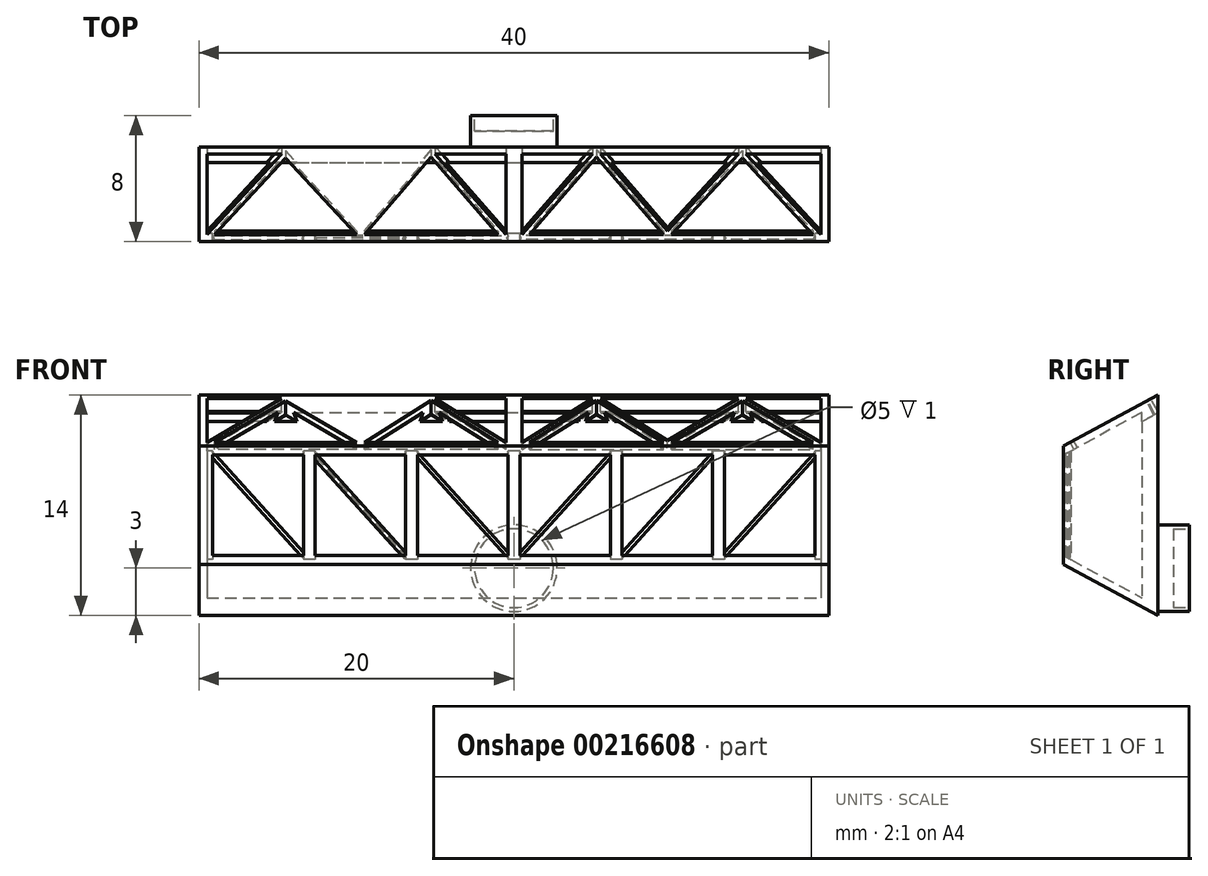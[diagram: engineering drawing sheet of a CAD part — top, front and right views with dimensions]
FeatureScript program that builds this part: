
annotation { "Feature Type Name" : "Feature", "Feature Type Description" : "" }
export const myFeature = defineFeature(function(context is Context, id is Id, definition is map)
    precondition{}
    {
        {
            var Q0;
            Q0=qCreatedBy(makeId("Right.planeOp"),FACE);
            var sketch = newSketch(context, id + "F0", { "sketchPlane" : qUnion([Q0])});
            skLineSegment(sketch, "E0", {"start": v(0, 0) * mm, "end": v(0, 7) * mm});
            skLineSegment(sketch, "E1", {"start": v(0, 0) * mm, "end": v(0, -7) * mm});
            skLineSegment(sketch, "E2", {"start": v(0, 0) * mm, "end": v(-6, 0) * mm});
            skLineSegment(sketch, "E3", {"start": v(-6, 0) * mm, "end": v(-6, 3.75) * mm});
            skLineSegment(sketch, "E4", {"start": v(-6, 3.75) * mm, "end": v(0, 7) * mm});
            skLineSegment(sketch, "E5.MirrorCS", {"start": v(-6, 0) * mm, "end": v(-6, -3.75) * mm});
            skLineSegment(sketch, "E6", {"start": v(-6, -3.75) * mm, "end": v(0, -7) * mm});
            skSolve(sketch);
        }
        {
            var Q0;
            Q0=makeQuery(id+"F0.imprint","IMPRINT",FACE,{"disambiguationData":[TD([[makeQuery(id+"F0.imprint","IMPRINT",EDGE,{"derivedFrom":sQuery(id+"F0.wireOp",EDGE,"E2")}),1.0]])]});
            var Q1;
            Q1=makeQuery(id+"F0.imprint","IMPRINT",FACE,{"disambiguationData":[TD([[makeQuery(id+"F0.imprint","IMPRINT",EDGE,{"derivedFrom":sQuery(id+"F0.wireOp",EDGE,"E0")}),1.0]])]});
            var Q2;
            Q2=sQuery(id+"F0.wireOp",EDGE,"E4");
            var Q3;
            Q3=sQuery(id+"F0.wireOp",EDGE,"E0");
            var Q4;
            Q4=sQuery(id+"F0.wireOp",EDGE,"E3");
            var Q5;
            Q5=sQuery(id+"F0.wireOp",EDGE,"E5.MirrorCS");
            var Q6;
            Q6=sQuery(id+"F0.wireOp",EDGE,"E1");
            var Q7;
            Q7=sQuery(id+"F0.wireOp",EDGE,"E6");
            extrude(context, id + "F1", {"entities" : qUnion([Q0, Q1]), "surfaceEntities" : qUnion([Q2, Q3, Q4, Q5, Q6, Q7]), "depth" : 20 * mm, "hasSecondDirection" : true, "secondDirectionOppositeDirection" : true, "secondDirectionDepth" : 20 * mm});
        }
        {
            var Q0;
            Q0=makeQuery(id+"F1.opExtrude","SWEPT_FACE",FACE,{"disambiguationData":[OSD([sQuery(id+"F0.wireOp",EDGE,"E0"),sQuery(id+"F0.wireOp",EDGE,"5257f137-ee3b-4e42-818e-476b2dafb2f60.MirrorCS")])]});
            var sketch = newSketch(context, id + "F2", { "sketchPlane" : qUnion([Q0])});
            skLineSegment(sketch, "E7", {"start": v(0, -7) * mm, "end": v(0, -4) * mm});
            skPoint(sketch, "E7.endSnap0", {"position": v(0, -7) * mm});
            skCircle(sketch, "E8", {"center": v(0, -4) * mm, "radius": 2.75 * mm});
            skSolve(sketch);
        }
        {
            var Q0;
            Q0=makeQuery(id+"F2.imprint","IMPRINT",FACE,{"disambiguationData":[TD([[makeQuery(id+"F2.imprint","IMPRINT",EDGE,{"derivedFrom":sQuery(id+"F2.wireOp",EDGE,"E8")}),1.0]])]});
            extrude(context, id + "F3", {"entities" : qUnion([Q0]), "operationType" : NewBodyOperationType.ADD, "depth" : 2 * mm});
        }
        {
            var Q0;
            Q0=qCreatedBy(makeId("Right.planeOp"),FACE);
            var sketch = newSketch(context, id + "F4", { "sketchPlane" : qUnion([Q0])});
            skLineSegment(sketch, "E9", {"start": v(-2.76, 4.94) * mm, "end": v(-1, 5.9) * mm});
            skLineSegment(sketch, "E10", {"start": v(-2.76, 4.94) * mm, "end": v(-6, 3.19) * mm});
            skLineSegment(sketch, "E11", {"start": v(-1, 0) * mm, "end": v(-1, -5.89) * mm});
            skLineSegment(sketch, "E12", {"start": v(-1, 5.9) * mm, "end": v(-1, 0) * mm});
            skLineSegment(sketch, "E13", {"start": v(-6, -3.19) * mm, "end": v(-1, -5.89) * mm});
            skLineSegment(sketch, "E14", {"start": v(-6, 3.19) * mm, "end": v(-6, -3.19) * mm});
            skSolve(sketch);
        }
        {
            var Q0;
            Q0=makeQuery(id+"F4.imprint","IMPRINT",FACE,{"disambiguationData":[TD([[makeQuery(id+"F4.imprint","IMPRINT",EDGE,{"derivedFrom":sQuery(id+"F4.wireOp",EDGE,"E9")}),-1.0]])]});
            extrude(context, id + "F5", {"entities" : qUnion([Q0]), "operationType" : NewBodyOperationType.REMOVE, "oppositeDirection" : true, "depth" : 19.5 * mm, "hasSecondDirection" : true, "secondDirectionOppositeDirection" : false, "secondDirectionDepth" : 19.5 * mm});
        }
        {
            var Q0;
            Q0=makeQuery(id+"F1.opExtrude","SWEPT_FACE",FACE,{"disambiguationData":[OSD([sQuery(id+"F0.wireOp",EDGE,"E3"),sQuery(id+"F0.wireOp",EDGE,"E5.MirrorCS")])]});
            var sketch = newSketch(context, id + "F6", { "sketchPlane" : qUnion([Q0])});
            skLineSegment(sketch, "E15", {"start": v(0, 0) * mm, "end": v(0, 9.2) * mm, "construction": true});
            skPoint(sketch, "E15.endSnap0", {"position": v(0, 3.75) * mm});
            skLineSegment(sketch, "E16.bottom", {"start": v(0, 3.75) * mm, "end": v(-0.38, 3.75) * mm});
            skLineSegment(sketch, "E16.top", {"start": v(0, -3.75) * mm, "end": v(-0.37, -3.75) * mm});
            skLineSegment(sketch, "E16.left", {"start": v(0, 3.75) * mm, "end": v(0, -3.75) * mm});
            skLineSegment(sketch, "E16.right", {"start": v(-0.38, 3.75) * mm, "end": v(-0.37, -3.75) * mm});
            skLineSegment(sketch, "E17.bottom", {"start": v(0, 3.75) * mm, "end": v(0.38, 3.75) * mm});
            skLineSegment(sketch, "E17.top", {"start": v(0, -3.75) * mm, "end": v(0.38, -3.75) * mm});
            skLineSegment(sketch, "E17.right", {"start": v(0.38, 3.75) * mm, "end": v(0.38, -3.75) * mm});
            skLineSegment(sketch, "E18.trimOffspring", {"start": v(0, 0) * mm, "end": v(0, -10.66) * mm, "construction": true});
            skLineSegment(sketch, "E19.1.0.0", {"start": v(6.5, 3.75) * mm, "end": v(6.5, -3.75) * mm});
            skLineSegment(sketch, "E19.1.0.1", {"start": v(6.88, 3.75) * mm, "end": v(6.88, -3.75) * mm});
            skLineSegment(sketch, "E19.1.0.2", {"start": v(6.13, 3.75) * mm, "end": v(6.13, -3.75) * mm});
            skPoint(sketch, "E19.1.0.3", {"position": v(6.5, 3.75) * mm});
            skLineSegment(sketch, "E19.1.0.4", {"start": v(6.5, 3.75) * mm, "end": v(6.5, -3.75) * mm});
            skLineSegment(sketch, "E19.1.0.5", {"start": v(6.5, -3.75) * mm, "end": v(6.88, -3.75) * mm});
            skLineSegment(sketch, "E19.1.0.6", {"start": v(6.5, 3.75) * mm, "end": v(6.12, 3.75) * mm});
            skLineSegment(sketch, "E19.1.0.7", {"start": v(6.5, -3.75) * mm, "end": v(6.13, -3.75) * mm});
            skLineSegment(sketch, "E19.1.0.8", {"start": v(6.5, 3.75) * mm, "end": v(6.88, 3.75) * mm});
            skLineSegment(sketch, "E19.2.0.0", {"start": v(13, 3.75) * mm, "end": v(13, -3.75) * mm});
            skLineSegment(sketch, "E19.2.0.1", {"start": v(13.38, 3.75) * mm, "end": v(13.38, -3.75) * mm});
            skLineSegment(sketch, "E19.2.0.2", {"start": v(12.62, 3.75) * mm, "end": v(12.63, -3.75) * mm});
            skPoint(sketch, "E19.2.0.3", {"position": v(13, 3.75) * mm});
            skLineSegment(sketch, "E19.2.0.4", {"start": v(13, 3.75) * mm, "end": v(13, -3.75) * mm});
            skLineSegment(sketch, "E19.2.0.5", {"start": v(13, -3.75) * mm, "end": v(13.38, -3.75) * mm});
            skLineSegment(sketch, "E19.2.0.6", {"start": v(13, 3.75) * mm, "end": v(12.62, 3.75) * mm});
            skLineSegment(sketch, "E19.2.0.7", {"start": v(13, -3.75) * mm, "end": v(12.63, -3.75) * mm});
            skLineSegment(sketch, "E19.2.0.8", {"start": v(13, 3.75) * mm, "end": v(13.38, 3.75) * mm});
            skLineSegment(sketch, "E19.3.0.0", {"start": v(19.5, 3.75) * mm, "end": v(19.5, -3.75) * mm});
            skLineSegment(sketch, "E19.3.0.1", {"start": v(19.88, 3.75) * mm, "end": v(19.88, -3.75) * mm});
            skLineSegment(sketch, "E19.3.0.2", {"start": v(19.13, 3.75) * mm, "end": v(19.13, -3.75) * mm});
            skPoint(sketch, "E19.3.0.3", {"position": v(19.5, 3.75) * mm});
            skLineSegment(sketch, "E19.3.0.4", {"start": v(19.5, 3.75) * mm, "end": v(19.5, -3.75) * mm});
            skLineSegment(sketch, "E19.3.0.5", {"start": v(19.5, -3.75) * mm, "end": v(19.88, -3.75) * mm});
            skLineSegment(sketch, "E19.3.0.6", {"start": v(19.5, 3.75) * mm, "end": v(19.13, 3.75) * mm});
            skLineSegment(sketch, "E19.3.0.7", {"start": v(19.5, -3.75) * mm, "end": v(19.13, -3.75) * mm});
            skLineSegment(sketch, "E19.3.0.8", {"start": v(19.5, 3.75) * mm, "end": v(19.88, 3.75) * mm});
            skLineSegment(sketch, "E19.direction1", {"start": v(-0.37, -3.75) * mm, "end": v(6.13, -3.75) * mm, "construction": true});
            skLineSegment(sketch, "E20.1.0.0", {"start": v(-6.88, 3.75) * mm, "end": v(-6.87, -3.75) * mm});
            skLineSegment(sketch, "E20.1.0.1", {"start": v(-6.5, 3.75) * mm, "end": v(-6.5, -3.75) * mm});
            skLineSegment(sketch, "E20.1.0.2", {"start": v(-6.12, 3.75) * mm, "end": v(-6.12, -3.75) * mm});
            skPoint(sketch, "E20.1.0.3", {"position": v(-6.5, 3.75) * mm});
            skLineSegment(sketch, "E20.1.0.4", {"start": v(-6.5, 3.75) * mm, "end": v(-6.5, -3.75) * mm});
            skLineSegment(sketch, "E20.1.0.5", {"start": v(-6.5, 3.75) * mm, "end": v(-6.88, 3.75) * mm});
            skLineSegment(sketch, "E20.1.0.6", {"start": v(-6.5, 3.75) * mm, "end": v(-6.12, 3.75) * mm});
            skLineSegment(sketch, "E20.1.0.7", {"start": v(-6.5, -3.75) * mm, "end": v(-6.12, -3.75) * mm});
            skLineSegment(sketch, "E20.1.0.8", {"start": v(-6.5, -3.75) * mm, "end": v(-6.87, -3.75) * mm});
            skLineSegment(sketch, "E20.2.0.0", {"start": v(-13.38, 3.75) * mm, "end": v(-13.37, -3.75) * mm});
            skLineSegment(sketch, "E20.2.0.1", {"start": v(-13, 3.75) * mm, "end": v(-13, -3.75) * mm});
            skLineSegment(sketch, "E20.2.0.2", {"start": v(-12.62, 3.75) * mm, "end": v(-12.62, -3.75) * mm});
            skPoint(sketch, "E20.2.0.3", {"position": v(-13, 3.75) * mm});
            skLineSegment(sketch, "E20.2.0.4", {"start": v(-13, 3.75) * mm, "end": v(-13, -3.75) * mm});
            skLineSegment(sketch, "E20.2.0.5", {"start": v(-13, 3.75) * mm, "end": v(-13.38, 3.75) * mm});
            skLineSegment(sketch, "E20.2.0.6", {"start": v(-13, 3.75) * mm, "end": v(-12.62, 3.75) * mm});
            skLineSegment(sketch, "E20.2.0.7", {"start": v(-13, -3.75) * mm, "end": v(-12.62, -3.75) * mm});
            skLineSegment(sketch, "E20.2.0.8", {"start": v(-13, -3.75) * mm, "end": v(-13.37, -3.75) * mm});
            skLineSegment(sketch, "E20.3.0.0", {"start": v(-19.88, 3.75) * mm, "end": v(-19.88, -3.75) * mm});
            skLineSegment(sketch, "E20.3.0.1", {"start": v(-19.5, 3.75) * mm, "end": v(-19.5, -3.75) * mm});
            skLineSegment(sketch, "E20.3.0.2", {"start": v(-19.13, 3.75) * mm, "end": v(-19.13, -3.75) * mm});
            skPoint(sketch, "E20.3.0.3", {"position": v(-19.5, 3.75) * mm});
            skLineSegment(sketch, "E20.3.0.4", {"start": v(-19.5, 3.75) * mm, "end": v(-19.5, -3.75) * mm});
            skLineSegment(sketch, "E20.3.0.5", {"start": v(-19.5, 3.75) * mm, "end": v(-19.88, 3.75) * mm});
            skLineSegment(sketch, "E20.3.0.6", {"start": v(-19.5, 3.75) * mm, "end": v(-19.13, 3.75) * mm});
            skLineSegment(sketch, "E20.3.0.7", {"start": v(-19.5, -3.75) * mm, "end": v(-19.13, -3.75) * mm});
            skLineSegment(sketch, "E20.3.0.8", {"start": v(-19.5, -3.75) * mm, "end": v(-19.88, -3.75) * mm});
            skLineSegment(sketch, "E20.direction1", {"start": v(-0.37, -3.75) * mm, "end": v(-6.87, -3.75) * mm, "construction": true});
            skSolve(sketch);
        }
        {
            var Q0;
            Q0 = qSketchRegion(id + "F6", true);
            extrude(context, id + "F7", {"entities" : qUnion([Q0]), "operationType" : NewBodyOperationType.ADD, "oppositeDirection" : true, "depth" : .5 * mm});
        }
        {
            var Q0;
            Q0=qCreatedBy(makeId("Front.planeOp"),FACE);
            cPlane(context, id + "F8", {"entities" : qUnion([Q0]), "cplaneType" : CPlaneType.OFFSET, "offset" : 5.75 * mm, "width" : 150 * mm, "height" : 150 * mm});
        }
        {
            var Q0;
            Q0=qCreatedBy(id+"F8.planeOp",FACE);
            var sketch = newSketch(context, id + "F9", { "sketchPlane" : qUnion([Q0])});
            skLineSegment(sketch, "E21", {"start": v(-0.38, -3.18) * mm, "end": v(-0.18, -3.4) * mm});
            skLineSegment(sketch, "E22", {"start": v(-0.18, -3.4) * mm, "end": v(-0.09, -3.32) * mm});
            skLineSegment(sketch, "E23", {"start": v(-0.18, -3.4) * mm, "end": v(-0.27, -3.48) * mm});
            skLineSegment(sketch, "E24", {"start": v(-6.18, 3.43) * mm, "end": v(-0.09, -3.32) * mm});
            skLineSegment(sketch, "E25.MirrorCS", {"start": v(0.18, -3.4) * mm, "end": v(0.09, -3.32) * mm});
            skLineSegment(sketch, "E26.MirrorCS", {"start": v(0.18, -3.4) * mm, "end": v(0.27, -3.48) * mm});
            skLineSegment(sketch, "E27.MirrorCS", {"start": v(6.37, 3.27) * mm, "end": v(6.18, 3.43) * mm});
            skLineSegment(sketch, "E28.MirrorCS", {"start": v(0.38, -3.18) * mm, "end": v(0.18, -3.4) * mm});
            skLineSegment(sketch, "E29.MirrorCS", {"start": v(6.18, 3.43) * mm, "end": v(0.09, -3.32) * mm});
            skLineSegment(sketch, "E30.1.0.1", {"start": v(-12.68, 3.43) * mm, "end": v(-6.59, -3.32) * mm});
            skLineSegment(sketch, "E30.1.0.2", {"start": v(-12.87, 3.27) * mm, "end": v(-12.68, 3.43) * mm});
            skLineSegment(sketch, "E30.1.0.3", {"start": v(-6.88, -3.18) * mm, "end": v(-6.68, -3.4) * mm});
            skLineSegment(sketch, "E30.1.0.5", {"start": v(-6.68, -3.4) * mm, "end": v(-6.59, -3.32) * mm});
            skLineSegment(sketch, "E30.2.0.1", {"start": v(-19.18, 3.43) * mm, "end": v(-13.09, -3.32) * mm});
            skLineSegment(sketch, "E30.2.0.3", {"start": v(-13.38, -3.18) * mm, "end": v(-13.18, -3.4) * mm});
            skLineSegment(sketch, "E30.2.0.4", {"start": v(-13.18, -3.4) * mm, "end": v(-13.27, -3.48) * mm});
            skLineSegment(sketch, "E30.2.0.5", {"start": v(-13.18, -3.4) * mm, "end": v(-13.09, -3.32) * mm});
            skLineSegment(sketch, "E30.direction1", {"start": v(-0.27, -3.48) * mm, "end": v(-6.77, -3.48) * mm, "construction": true});
            skLineSegment(sketch, "E31.1.0.1", {"start": v(12.68, 3.43) * mm, "end": v(6.59, -3.32) * mm});
            skLineSegment(sketch, "E31.1.0.2", {"start": v(12.87, 3.27) * mm, "end": v(12.68, 3.43) * mm});
            skLineSegment(sketch, "E31.1.0.3", {"start": v(6.88, -3.18) * mm, "end": v(6.68, -3.4) * mm});
            skLineSegment(sketch, "E31.1.0.4", {"start": v(6.68, -3.4) * mm, "end": v(6.77, -3.48) * mm});
            skLineSegment(sketch, "E31.1.0.5", {"start": v(6.68, -3.4) * mm, "end": v(6.59, -3.32) * mm});
            skLineSegment(sketch, "E31.2.0.1", {"start": v(19.18, 3.43) * mm, "end": v(13.09, -3.32) * mm});
            skLineSegment(sketch, "E31.2.0.2", {"start": v(19.37, 3.27) * mm, "end": v(19.18, 3.43) * mm});
            skLineSegment(sketch, "E31.2.0.3", {"start": v(13.38, -3.18) * mm, "end": v(13.18, -3.4) * mm});
            skLineSegment(sketch, "E31.2.0.4", {"start": v(13.18, -3.4) * mm, "end": v(13.27, -3.48) * mm});
            skLineSegment(sketch, "E31.2.0.5", {"start": v(13.18, -3.4) * mm, "end": v(13.09, -3.32) * mm});
            skLineSegment(sketch, "E31.direction1", {"start": v(0.09, -3.32) * mm, "end": v(6.59, -3.32) * mm, "construction": true});
            skLineSegment(sketch, "E32", {"start": v(-19.67, -3.5) * mm, "end": v(-19.57, -3.43) * mm});
            skLineSegment(sketch, "E33", {"start": v(-19.67, -3.5) * mm, "end": v(-19.78, -3.57) * mm});
            skLineSegment(sketch, "E34", {"start": v(-13.38, -3.18) * mm, "end": v(-19.28, 3.35) * mm});
            skLineSegment(sketch, "E35", {"start": v(-19.18, 3.43) * mm, "end": v(-19.28, 3.35) * mm});
            skLineSegment(sketch, "E36", {"start": v(-6.88, -3.18) * mm, "end": v(-12.75, 3.27) * mm});
            skLineSegment(sketch, "E37", {"start": v(-12.75, 3.27) * mm, "end": v(-12.8, 3.33) * mm});
            skLineSegment(sketch, "E38", {"start": v(-0.38, -3.18) * mm, "end": v(-6.28, 3.35) * mm});
            skLineSegment(sketch, "E39", {"start": v(-6.18, 3.43) * mm, "end": v(-6.28, 3.35) * mm});
            skLineSegment(sketch, "E40", {"start": v(0.38, -3.18) * mm, "end": v(6.28, 3.35) * mm});
            skLineSegment(sketch, "E41", {"start": v(6.88, -3.18) * mm, "end": v(12.78, 3.35) * mm});
            skLineSegment(sketch, "E42", {"start": v(13.38, -3.18) * mm, "end": v(19.28, 3.35) * mm});
            skSolve(sketch);
        }
        {
            var Q0;
            Q0=makeQuery(id+"F9.imprint","IMPRINT",FACE,{"disambiguationData":[TD([[makeQuery(id+"F9.imprint","IMPRINT",EDGE,{"derivedFrom":sQuery(id+"F9.wireOp",EDGE,"E30.2.0.1")}),-1.0]])]});
            var Q1;
            Q1=sQuery(id+"F9.wireOp",EDGE,"E34");
            revolve(context, id + "F10", {"operationType" : NewBodyOperationType.ADD, "entities" : qUnion([Q0]), "axis" : qUnion([Q1]), "revolveType" : RevolveType.FULL});
        }
        {
            var Q0;
            {var subQ1=sQuery(id+"F9.wireOp",EDGE,"E30.1.0.1");Q0=makeQuery(id+"F9.imprint","IMPRINT",FACE,{"disambiguationData":[TD([[makeQuery(id+"F9.imprint","IMPRINT",EDGE,{"derivedFrom":subQ1}),-1.0]])]});}
            var Q1;
            Q1=sQuery(id+"F9.wireOp",EDGE,"E37");
            revolve(context, id + "F11", {"operationType" : NewBodyOperationType.ADD, "entities" : qUnion([Q0]), "axis" : qUnion([Q1]), "revolveType" : RevolveType.FULL});
        }
        {
            var Q0;
            Q0=makeQuery(id+"F9.imprint","IMPRINT",FACE,{"disambiguationData":[TD([[makeQuery(id+"F9.imprint","IMPRINT",EDGE,{"derivedFrom":sQuery(id+"F9.wireOp",EDGE,"E21")}),1.0]])]});
            var Q1;
            Q1=sQuery(id+"F9.wireOp",EDGE,"E38");
            revolve(context, id + "F12", {"operationType" : NewBodyOperationType.ADD, "entities" : qUnion([Q0]), "axis" : qUnion([Q1]), "revolveType" : RevolveType.FULL});
        }
        {
            var Q0;
            Q0=makeQuery(id+"F9.imprint","IMPRINT",FACE,{"disambiguationData":[TD([[makeQuery(id+"F9.imprint","IMPRINT",EDGE,{"derivedFrom":sQuery(id+"F9.wireOp",EDGE,"E25.MirrorCS")}),-1.0]])]});
            var Q1;
            Q1=sQuery(id+"F9.wireOp",EDGE,"E40");
            revolve(context, id + "F13", {"operationType" : NewBodyOperationType.ADD, "entities" : qUnion([Q0]), "axis" : qUnion([Q1]), "revolveType" : RevolveType.FULL});
        }
        {
            var Q0;
            {var subQ1=sQuery(id+"F9.wireOp",EDGE,"E31.1.0.1");Q0=makeQuery(id+"F9.imprint","IMPRINT",FACE,{"disambiguationData":[TD([[makeQuery(id+"F9.imprint","IMPRINT",EDGE,{"derivedFrom":subQ1}),1.0]])]});}
            var Q1;
            Q1=sQuery(id+"F9.wireOp",EDGE,"E41");
            revolve(context, id + "F14", {"operationType" : NewBodyOperationType.ADD, "entities" : qUnion([Q0]), "axis" : qUnion([Q1]), "revolveType" : RevolveType.FULL});
        }
        {
            var Q0;
            {var subQ1=sQuery(id+"F9.wireOp",EDGE,"E31.2.0.1");Q0=makeQuery(id+"F9.imprint","IMPRINT",FACE,{"disambiguationData":[TD([[makeQuery(id+"F9.imprint","IMPRINT",EDGE,{"derivedFrom":subQ1}),1.0]])]});}
            var Q1;
            Q1=sQuery(id+"F9.wireOp",EDGE,"E42");
            revolve(context, id + "F15", {"operationType" : NewBodyOperationType.ADD, "entities" : qUnion([Q0]), "axis" : qUnion([Q1]), "revolveType" : RevolveType.FULL});
        }
        {
            var Q0;
            Q0=makeQuery(id+"F1.opExtrude","SWEPT_FACE",FACE,{"disambiguationData":[OSD([sQuery(id+"F0.wireOp",EDGE,"E4")])]});
            var sketch = newSketch(context, id + "F16", { "sketchPlane" : qUnion([Q0])});
            skLineSegment(sketch, "E43", {"start": v(-20, 3.33) * mm, "end": v(-19.5, 3.33) * mm});
            skLineSegment(sketch, "E44", {"start": v(-19.5, 2.83) * mm, "end": v(-19.5, -3.49) * mm});
            skLineSegment(sketch, "E45", {"start": v(0, 3.33) * mm, "end": v(-0.5, 3.33) * mm});
            skLineSegment(sketch, "E46", {"start": v(-0.5, 3.33) * mm, "end": v(-0.5, -2.99) * mm});
            skLineSegment(sketch, "E47", {"start": v(0, -3.49) * mm, "end": v(-0.5, -3.49) * mm});
            skLineSegment(sketch, "E48", {"start": v(-19.5, 3.33) * mm, "end": v(-0.5, 3.33) * mm});
            skLineSegment(sketch, "E49", {"start": v(-19.5, 2.83) * mm, "end": v(-5.25, 2.83) * mm});
            skLineSegment(sketch, "E50", {"start": v(-19.5, -3.49) * mm, "end": v(-19.5, -2.99) * mm});
            skLineSegment(sketch, "E51", {"start": v(-19.5, -2.99) * mm, "end": v(-10, -2.99) * mm});
            skLineSegment(sketch, "E52", {"start": v(-19.5, 2.83) * mm, "end": v(-14.75, 2.83) * mm});
            skLineSegment(sketch, "E53", {"start": v(-14.75, 2.83) * mm, "end": v(-7.5, 2.83) * mm});
            skLineSegment(sketch, "E54", {"start": v(-0.5, 2.83) * mm, "end": v(-5, 2.83) * mm});
            skLineSegment(sketch, "E55", {"start": v(-14.75, 2.83) * mm, "end": v(-14.25, 2.83) * mm});
            skLineSegment(sketch, "E56", {"start": v(-14.25, 2.83) * mm, "end": v(-8.25, 2.83) * mm});
            skLineSegment(sketch, "E57", {"start": v(-8.25, 2.83) * mm, "end": v(-5.25, 2.83) * mm});
            skLineSegment(sketch, "E58", {"start": v(-19.5, -2.99) * mm, "end": v(-19, -2.99) * mm});
            skLineSegment(sketch, "E59", {"start": v(-19, -2.99) * mm, "end": v(-10, -2.99) * mm});
            skLineSegment(sketch, "E60", {"start": v(-19.5, -2.99) * mm, "end": v(-14.75, 2.83) * mm});
            skLineSegment(sketch, "E61", {"start": v(-19, -2.99) * mm, "end": v(-14.5, 2.53) * mm});
            skPoint(sketch, "E61.endSnap0", {"position": v(-14.5, 2.83) * mm});
            skLineSegment(sketch, "E62", {"start": v(-9.75, -2.99) * mm, "end": v(-9.5, -2.99) * mm});
            skLineSegment(sketch, "E63", {"start": v(-14.5, 2.53) * mm, "end": v(-10, -2.99) * mm});
            skLineSegment(sketch, "E64", {"start": v(-9.75, -2.75) * mm, "end": v(-14.25, 2.83) * mm});
            skLineSegment(sketch, "E65", {"start": v(-19.25, -2.99) * mm, "end": v(-10, -2.99) * mm});
            skLineSegment(sketch, "E66", {"start": v(-5.25, 2.83) * mm, "end": v(-5.5, 2.83) * mm});
            skLineSegment(sketch, "E67", {"start": v(-5.5, 2.83) * mm, "end": v(-5.25, 2.83) * mm});
            skLineSegment(sketch, "E68", {"start": v(-9.75, -2.75) * mm, "end": v(-5.5, 2.83) * mm});
            skLineSegment(sketch, "E69", {"start": v(-5.25, 2.6) * mm, "end": v(-9.5, -2.99) * mm});
            skLineSegment(sketch, "E70", {"start": v(-1, -2.99) * mm, "end": v(-5.25, 2.6) * mm});
            skLineSegment(sketch, "E71", {"start": v(-5, 2.83) * mm, "end": v(-0.5, -2.99) * mm});
            skLineSegment(sketch, "E72.MirrorCS", {"start": v(5.25, 2.83) * mm, "end": v(5.5, 2.83) * mm});
            skLineSegment(sketch, "E73.MirrorCS", {"start": v(19.25, -2.99) * mm, "end": v(19, -2.99) * mm});
            skLineSegment(sketch, "E74.MirrorCS", {"start": v(19.5, 3.33) * mm, "end": v(19.5, 2.83) * mm});
            skLineSegment(sketch, "E75.MirrorCS", {"start": v(0, -3.49) * mm, "end": v(0.5, -3.49) * mm});
            skLineSegment(sketch, "E76.MirrorCS", {"start": v(0, 3.33) * mm, "end": v(0.5, 3.33) * mm});
            skLineSegment(sketch, "E77.MirrorCS", {"start": v(19.25, -2.99) * mm, "end": v(10, -2.99) * mm});
            skLineSegment(sketch, "E78.MirrorCS", {"start": v(8.25, 2.83) * mm, "end": v(5.25, 2.83) * mm});
            skLineSegment(sketch, "E79.MirrorCS", {"start": v(0.5, 2.83) * mm, "end": v(5, 2.83) * mm});
            skLineSegment(sketch, "E80.MirrorCS", {"start": v(14.25, 2.83) * mm, "end": v(8.25, 2.83) * mm});
            skLineSegment(sketch, "E81.MirrorCS", {"start": v(20, 3.33) * mm, "end": v(19.5, 3.33) * mm});
            skLineSegment(sketch, "E82.MirrorCS", {"start": v(19.5, -2.99) * mm, "end": v(14.75, 2.83) * mm});
            skLineSegment(sketch, "E83.MirrorCS", {"start": v(1, -2.99) * mm, "end": v(5.25, 2.6) * mm});
            skLineSegment(sketch, "E84.MirrorCS", {"start": v(19, -2.99) * mm, "end": v(10, -2.99) * mm});
            skLineSegment(sketch, "E85.MirrorCS", {"start": v(14.5, 2.53) * mm, "end": v(10, -2.99) * mm});
            skLineSegment(sketch, "E86.MirrorCS", {"start": v(9.75, -2.75) * mm, "end": v(14.25, 2.83) * mm});
            skLineSegment(sketch, "E87.MirrorCS", {"start": v(9.75, -2.75) * mm, "end": v(5.5, 2.83) * mm});
            skLineSegment(sketch, "E88.MirrorCS", {"start": v(0.5, 2.83) * mm, "end": v(0.5, -2.99) * mm});
            skLineSegment(sketch, "E89.MirrorCS", {"start": v(19.5, 3.33) * mm, "end": v(0.5, 3.33) * mm});
            skLineSegment(sketch, "E90.MirrorCS", {"start": v(5, 2.83) * mm, "end": v(0.5, -2.99) * mm});
            skLineSegment(sketch, "E91.MirrorCS", {"start": v(14.5, 2.83) * mm, "end": v(7.5, 2.83) * mm});
            skPoint(sketch, "E92.MirrorP", {"position": v(14.5, 2.83) * mm});
            skLineSegment(sketch, "E93.MirrorCS", {"start": v(19.5, 3.33) * mm, "end": v(19.5, -2.99) * mm});
            skLineSegment(sketch, "E94.MirrorCS", {"start": v(19.5, 2.83) * mm, "end": v(14.75, 2.83) * mm});
            skLineSegment(sketch, "E95.MirrorCS", {"start": v(5.25, 2.6) * mm, "end": v(9.5, -2.99) * mm});
            skLineSegment(sketch, "E96.MirrorCS", {"start": v(19, -2.99) * mm, "end": v(14.5, 2.53) * mm});
            skLineSegment(sketch, "E97.trimOffspring", {"start": v(-5, 2.83) * mm, "end": v(-0.5, 2.83) * mm});
            skLineSegment(sketch, "E98", {"start": v(-9.5, -2.99) * mm, "end": v(-1, -2.99) * mm});
            skLineSegment(sketch, "E99.trimOffspring", {"start": v(5, 2.83) * mm, "end": v(0.5, 2.83) * mm});
            skLineSegment(sketch, "E100.trimOffspring", {"start": v(9.5, -2.99) * mm, "end": v(0.5, -2.99) * mm});
            skLineSegment(sketch, "E101.trimOffspring", {"start": v(14.5, 2.83) * mm, "end": v(5.25, 2.83) * mm});
            skSolve(sketch);
        }
        {
            var Q0;
            {var subQ0=sQuery(id+"F16.wireOp",EDGE,"E86.MirrorCS");Q0=makeQuery(id+"F16.imprint","IMPRINT",FACE,{"disambiguationData":[TD([[makeQuery(id+"F16.imprint","IMPRINT",EDGE,{"derivedFrom":subQ0}),1.0]])]});}
            var Q1;
            {var subQ0=sQuery(id+"F16.wireOp",EDGE,"E85.MirrorCS");Q1=makeQuery(id+"F16.imprint","IMPRINT",FACE,{"disambiguationData":[TD([[makeQuery(id+"F16.imprint","IMPRINT",EDGE,{"derivedFrom":subQ0}),1.0]])]});}
            var Q2;
            {var subQ0=sQuery(id+"F16.wireOp",EDGE,"E82.MirrorCS");Q2=makeQuery(id+"F16.imprint","IMPRINT",FACE,{"disambiguationData":[TD([[makeQuery(id+"F16.imprint","IMPRINT",EDGE,{"derivedFrom":subQ0}),-1.0]])]});}
            var Q3;
            {var subQ0=sQuery(id+"F16.wireOp",EDGE,"E83.MirrorCS");Q3=makeQuery(id+"F16.imprint","IMPRINT",FACE,{"disambiguationData":[TD([[makeQuery(id+"F16.imprint","IMPRINT",EDGE,{"derivedFrom":subQ0}),-1.0]])]});}
            var Q4;
            Q4=makeQuery(id+"F16.imprint","IMPRINT",FACE,{"disambiguationData":[TD([[makeQuery(id+"F16.imprint","IMPRINT",EDGE,{"derivedFrom":sQuery(id+"F16.wireOp",EDGE,"E88.MirrorCS")}),1.0]])]});
            var Q5;
            {var subQ0=sQuery(id+"F16.wireOp",EDGE,"E71");Q5=makeQuery(id+"F16.imprint","IMPRINT",FACE,{"disambiguationData":[TD([[makeQuery(id+"F16.imprint","IMPRINT",EDGE,{"derivedFrom":subQ0}),1.0]])]});}
            var Q6;
            Q6=makeQuery(id+"F16.imprint","IMPRINT",FACE,{"disambiguationData":[TD([[makeQuery(id+"F16.imprint","IMPRINT",EDGE,{"derivedFrom":sQuery(id+"F16.wireOp",EDGE,"E69")}),1.0]])]});
            var Q7;
            {var subQ3=sQuery(id+"F16.wireOp",EDGE,"E56");Q7=makeQuery(id+"F16.imprint","IMPRINT",FACE,{"disambiguationData":[TD([[makeQuery(id+"F16.imprint","IMPRINT",EDGE,{"derivedFrom":subQ3}),-1.0]])]});}
            var Q8;
            {var subQ0=sQuery(id+"F16.wireOp",EDGE,"E61");Q8=makeQuery(id+"F16.imprint","IMPRINT",FACE,{"disambiguationData":[TD([[makeQuery(id+"F16.imprint","IMPRINT",EDGE,{"derivedFrom":subQ0}),-1.0]])]});}
            var Q9;
            Q9=makeQuery(id+"F16.imprint","IMPRINT",FACE,{"disambiguationData":[TD([[makeQuery(id+"F16.imprint","IMPRINT",EDGE,{"derivedFrom":sQuery(id+"F16.wireOp",EDGE,"E44")}),1.0]])]});
            extrude(context, id + "F17", {"entities" : qUnion([Q0, Q1, Q2, Q3, Q4, Q5, Q6, Q7, Q8, Q9]), "operationType" : NewBodyOperationType.REMOVE, "oppositeDirection" : true, "depth" : 1 * mm});
        }
        {
            var Q0;
            Q0=makeQuery(id+"F3.opExtrude","CAP_FACE",FACE,{"disambiguationData":[OSD([sQuery(id+"F2.wireOp",EDGE,"E8")])],"isStart":false});
            var sketch = newSketch(context, id + "F18", { "sketchPlane" : qUnion([Q0])});
            skLineSegment(sketch, "E102", {"start": v(0, 0) * mm, "end": v(0, -4) * mm});
            skCircle(sketch, "E103", {"center": v(0, -4) * mm, "radius": 2.5 * mm});
            skSolve(sketch);
        }
        {
            var Q0;
            Q0=makeQuery(id+"F18.imprint","IMPRINT",FACE,{"disambiguationData":[TD([[makeQuery(id+"F18.imprint","IMPRINT",EDGE,{"derivedFrom":sQuery(id+"F18.wireOp",EDGE,"E103")}),1.0]])]});
            extrude(context, id + "F19", {"entities" : qUnion([Q0]), "operationType" : NewBodyOperationType.REMOVE, "oppositeDirection" : true, "depth" : 1 * mm});
        }
    });
